FCSTD DOCUMENT  (FreeCAD 0.21R33668 +26 (Git))
Label: nibble_rev01
License: All rights reserved
LicenseURL: https://en.wikipedia.org/wiki/All_rights_reserved
objects: Sketcher::SketchObject×1
note: 1 computed .brp shape members not serialized (recipe doc carries the construction recipe); baked Part::Feature solids carry a one-line shape summary decoded from their .brp

FEATURE [Sketcher::SketchObject] Sketch
  FullyConstrained = true
  sketch-geometry (24):
    g0: LineSegment StartX=4e-16 StartY=4e-16 StartZ=0 EndX=6.5 EndY=-8e-16 EndZ=0
    g1: LineSegment StartX=6.5 StartY=-8e-16 StartZ=0 EndX=6.5 EndY=20 EndZ=0
    g2: LineSegment StartX=6.5 StartY=20 StartZ=0 EndX=18.5 EndY=20 EndZ=0
    g3: LineSegment StartX=18.5 StartY=20 StartZ=0 EndX=18.5 EndY=0 EndZ=0
    g4: LineSegment StartX=18.5 StartY=0 StartZ=0 EndX=25 EndY=-8e-16 EndZ=0
    g5: LineSegment StartX=25 StartY=-8e-16 StartZ=0 EndX=25 EndY=50 EndZ=0
    g6: LineSegment StartX=4e-16 StartY=4e-16 StartZ=0 EndX=0 EndY=50 EndZ=0
    g7: LineSegment StartX=6.5 StartY=50 StartZ=0 EndX=18.5 EndY=50 EndZ=0
    g8: ArcOfCircle CenterX=3.25 CenterY=0 CenterZ=0 NormalX=0 NormalY=0 NormalZ=1 AngleXU=0 Radius=3.25 StartAngle=3.14159 EndAngle=6.28319
    g9: ArcOfCircle CenterX=21.75 CenterY=0 CenterZ=0 NormalX=0 NormalY=0 NormalZ=1 AngleXU=0 Radius=3.25 StartAngle=3.14159 EndAngle=6.28319
    g10: ArcOfCircle CenterX=3.25 CenterY=55 CenterZ=0 NormalX=0 NormalY=0 NormalZ=1 AngleXU=0 Radius=0.75 StartAngle=0.436332 EndAngle=2.70526
    g11: LineSegment StartX=3.25 StartY=50 StartZ=0 EndX=3.25 EndY=55 EndZ=0
    g12: LineSegment StartX=0 StartY=50 StartZ=0 EndX=3.25 EndY=50 EndZ=0
    g13: LineSegment StartX=0 StartY=50 StartZ=0 EndX=2.57027 EndY=55.317 EndZ=0
    g14: LineSegment StartX=3.92973 StartY=55.317 StartZ=0 EndX=6.5 EndY=50 EndZ=0
    g15: LineSegment StartX=2.57027 StartY=55.317 StartZ=0 EndX=3.25 EndY=55 EndZ=0
    g16: LineSegment StartX=3.25 StartY=55 StartZ=0 EndX=3.92973 EndY=55.317 EndZ=0
    g17: LineSegment StartX=25 StartY=50 StartZ=0 EndX=21.75 EndY=50 EndZ=0
    g18: LineSegment StartX=21.75 StartY=50 StartZ=0 EndX=21.75 EndY=55 EndZ=0
    g19: ArcOfCircle CenterX=21.75 CenterY=55 CenterZ=0 NormalX=0 NormalY=0 NormalZ=1 AngleXU=0 Radius=0.75 StartAngle=0.436332 EndAngle=2.70526
    g20: LineSegment StartX=18.5 StartY=50 StartZ=0 EndX=21.0703 EndY=55.317 EndZ=0
    g21: LineSegment StartX=22.4297 StartY=55.317 StartZ=0 EndX=25 EndY=50 EndZ=0
    g22: LineSegment StartX=21.75 StartY=55 StartZ=0 EndX=22.4297 EndY=55.317 EndZ=0
    g23: LineSegment StartX=21.75 StartY=55 StartZ=0 EndX=21.0703 EndY=55.317 EndZ=0
  constraints (67):
    c: Coincident(g0,g-1)
    c: Coincident(g1,g0)
    c: Coincident(g2,g1)
    c: Coincident(g3,g2)
    c: Coincident(g4,g3)
    c: Coincident(g5,g4)
    c: Coincident(g6,g0)
    c: Distance(g0) = 6.5
    c: Distance(g4) = 6.5
    c: Perpendicular(g1,g0)
    c: Perpendicular(g0,g6)
    c: Perpendicular(g4,g3)
    c: Perpendicular(g5,g4)
    c: Perpendicular(g2,g1)
    c: Perpendicular(g3,g2)
    c: Parallel(g6,g-2)
    c: PointOnObject(g8,g0)
    c: Coincident(g8,g6)
    c: Coincident(g8,g1)
    c: PointOnObject(g9,g4)
    c: Coincident(g9,g3)
    c: Coincident(g9,g5)
    c: Distance(g2) = 12
    c: Distance(g6) = 50
    c: Distance(g5) = 50
    c: PointOnObject(g9,g-1)
    c: Distance(g1) = 20
    c: Parallel(g2,g7)
    c: DistanceX(g6,g7) = 6.5
    c: DistanceX(g7,g5) = 6.5
    c: Distance(g1,g7) = 30
    c: Coincident(g11,g10)
    c: Coincident(g12,g6)
    c: Coincident(g12,g11)
    c: Perpendicular(g6,g12)
    c: Perpendicular(g11,g12)
    c: Coincident(g13,g6)
    c: Coincident(g13,g10)
    c: Coincident(g14,g10)
    c: Coincident(g14,g7)
    c: Coincident(g15,g10)
    c: Coincident(g15,g10)
    c: Coincident(g16,g10)
    c: Coincident(g16,g10)
    c: Distance(g12) = 3.25
    c: Angle(g15,g11) = 2.00713
    c: Angle(g11,g16) = 2.00713
    c: Distance(g16) = 0.75
    c: DistanceY(g11,g11) = 5
    c: Coincident(g17,g5)
    c: Horizontal(g17)
    c: DistanceX(g17,g17) = 3.25
    c: Coincident(g18,g17)
    c: Vertical(g18)
    c: DistanceY(g18,g18) = 5
    c: Coincident(g19,g18)
    c: Coincident(g20,g7)
    c: Coincident(g20,g19)
    c: Coincident(g21,g19)
    c: Coincident(g21,g5)
    c: Coincident(g22,g19)
    c: Coincident(g22,g19)
    c: Coincident(g23,g19)
    c: Coincident(g23,g19)
    c: Angle(g23,g18) = 2.00713
    c: Angle(g18,g22) = 2.00713
    c: Distance(g22) = 0.75
